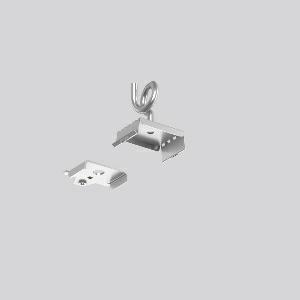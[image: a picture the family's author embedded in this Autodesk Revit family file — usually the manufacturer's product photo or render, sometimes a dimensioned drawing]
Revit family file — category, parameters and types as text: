
# Revit family: linedo_pendelset_ringose_982664_000_d89c
name_source: partatom
category: Lighting Fixtures
units: mm (PartAtom-declared; Revit-internal decimal feet)

## family parameters
Cut with Voids When Loaded = No
Host = Face
Light Source = No
Part Type = Normal
Room Calculation Point = No
Round Connector Dimension = Use Diameter
Shared = No

## types (1)
- LINEDO Pendelset Ringöse
    Apparent Load = 0 VA
    Default Elevation = 1800 mm
    Description = Suspension kit with open ring (chain not included). Spring steel, blank, for installing continuous line luminaire modules.
Colour: unpainted
Length: 33 mm
Width: 54 mm
Weight: 39,1 g
Type of Installation: pendant
    Height = 0 mm  [stored 0 ft]
    Lamp = 0 x
    Length = 33 mm
    Luminous efficacy = 0 lm/W
    Manufacturer = RZB
    ModVariant = No
    Model = 982664.000
    Mounting Place = Ceiling
    Mounting Type = Surface mounted
    Number of Poles = 1
    OnlyDefault = Yes
    Power Factor = 1
    Product Name = LINEDO Pendelset Ringöse
    Product group = Surface mounted continuous line luminaire system
    ProductGroupID = 310
    Protection Class = Protection class
    Protection Degree = Degree of protection
    RLX_Detail_Level = 1
    RLX_Emergency_Light_Flux = 0 lm
    RLX_Emergency_Type = 0
    RLX_Emergency_Type_DB = No
    RlxData = <blob elided: 10581 chars, md5=9644dc7e>
    Standby Power = 0 W
    System Light Flux = 0 lm
    System Power = 0 W
    Type Comments = Product without accessories
    Type Image = 982664.000.jpg
    URL = http://relux.com
    VarID = ---
    Voltage = 0 V
    Weight = 0.00 kg
    Width = 54 mm

note: [stored X ft] marks values corroborated as IEEE doubles in the binary element streams (Revit-internal decimal feet)

## geometry (parser evidence)
native form markers: Sweep x10
no freeform markers — native parametric forms only
